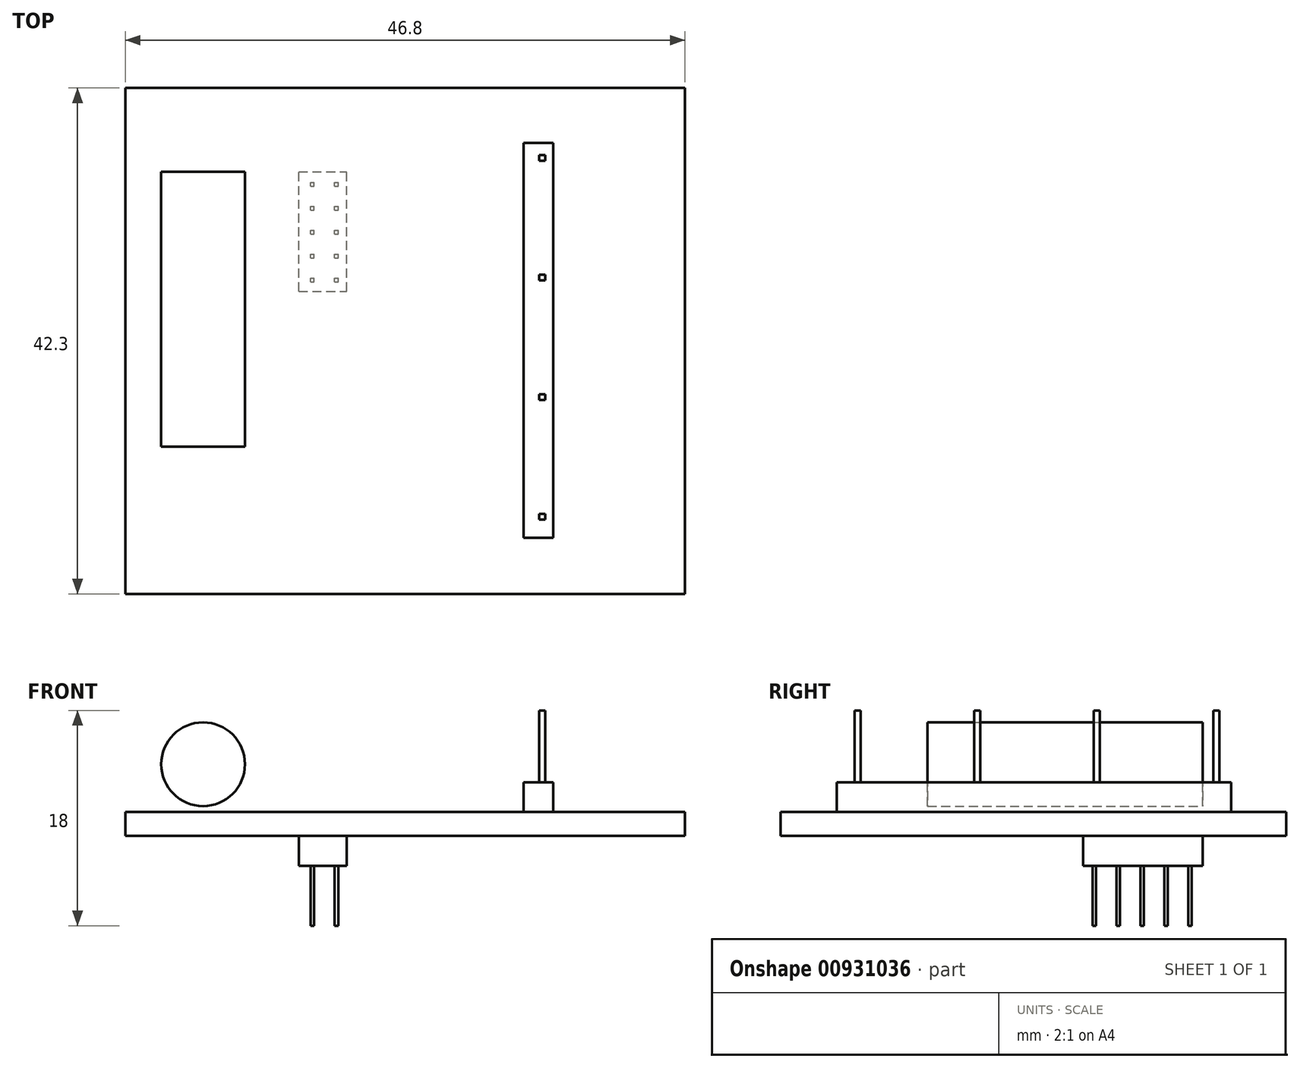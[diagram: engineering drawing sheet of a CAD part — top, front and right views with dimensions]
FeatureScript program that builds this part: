
annotation { "Feature Type Name" : "Feature", "Feature Type Description" : "" }
export const myFeature = defineFeature(function(context is Context, id is Id, definition is map)
    precondition{}
    {
        {
            assignVariable(context, id + "F0", {"name" : "PCB_WIDTH", "anyValue" : 42.3 * mm});
        }
        {
            assignVariable(context, id + "F1", {"name" : "PCB_HIGH", "anyValue" : 2 * mm});
        }
        {
            var Q0;
            Q0=qCreatedBy(makeId("Top.planeOp"),FACE);
            var sketch = newSketch(context, id + "F2", { "sketchPlane" : qUnion([Q0])});
            skLineSegment(sketch, "E0.bottom", {"start": v(-23.4, 21.15) * mm, "end": v(23.4, 21.15) * mm});
            skLineSegment(sketch, "E0.top", {"start": v(-23.4, -21.15) * mm, "end": v(23.4, -21.15) * mm});
            skLineSegment(sketch, "E0.left", {"start": v(-23.4, 21.15) * mm, "end": v(-23.4, -21.15) * mm});
            skLineSegment(sketch, "E0.right", {"start": v(23.4, 21.15) * mm, "end": v(23.4, -21.15) * mm});
            skLineSegment(sketch, "E1", {"start": v(-23.4, 21.15) * mm, "end": v(23.4, -21.15) * mm, "construction": true});
            skLineSegment(sketch, "E2", {"start": v(23.4, 21.15) * mm, "end": v(-23.4, -21.15) * mm, "construction": true});
            skPoint(sketch, "E3", {"position": v(0, 0) * mm});
            skSolve(sketch);
        }
        {
            var Q0;
            Q0 = qSketchRegion(id + "F2", true);
            extrude(context, id + "F3", {"entities" : qUnion([Q0]), "depth" : (getVariable(context, 'PCB_HIGH')), "offsetDistance" : 25 * mm});
        }
        {
            var Q0;
            Q0=qCreatedBy(makeId("Front.planeOp"),FACE);
            cPlane(context, id + "F4", {"entities" : qUnion([Q0]), "cplaneType" : CPlaneType.OFFSET, "offset" : (getVariable(context, 'PCB_WIDTH') / 2 - 7 * mm), "oppositeDirection" : true, "width" : 150 * mm, "height" : 150 * mm});
        }
        {
            var Q0;
            Q0=qCreatedBy(id+"F4.planeOp",FACE);
            var sketch = newSketch(context, id + "F5", { "sketchPlane" : qUnion([Q0])});
            skCircle(sketch, "E4", {"center": v(-16.9, 6) * mm, "radius": 3.5 * mm});
            skSolve(sketch);
        }
        {
            var Q0;
            Q0 = qSketchRegion(id + "F5", true);
            extrude(context, id + "F6", {"entities" : qUnion([Q0]), "depth" : 23 * mm, "offsetDistance" : 25 * mm});
        }
        {
            var Q0;
            Q0=makeQuery(id+"F3.opExtrude","CAP_FACE",FACE,{"disambiguationData":[OSD([sQuery(id+"F2.wireOp",EDGE,"E0.bottom"),sQuery(id+"F2.wireOp",EDGE,"E0.top"),sQuery(id+"F2.wireOp",EDGE,"E0.left"),sQuery(id+"F2.wireOp",EDGE,"E0.right")])],"isStart":false});
            var sketch = newSketch(context, id + "F7", { "sketchPlane" : qUnion([Q0])});
            skLineSegment(sketch, "E5.bottom", {"start": v(9.9, 16.55) * mm, "end": v(12.4, 16.55) * mm});
            skLineSegment(sketch, "E5.top", {"start": v(9.9, -16.45) * mm, "end": v(12.4, -16.45) * mm});
            skLineSegment(sketch, "E5.left", {"start": v(9.9, 16.55) * mm, "end": v(9.9, -16.45) * mm});
            skLineSegment(sketch, "E5.right", {"start": v(12.4, 16.55) * mm, "end": v(12.4, -16.45) * mm});
            skSolve(sketch);
        }
        {
            var Q0;
            Q0 = qSketchRegion(id + "F7", true);
            extrude(context, id + "F8", {"entities" : qUnion([Q0]), "depth" : 2.5 * mm, "offsetDistance" : 25 * mm});
        }
        {
            var Q0;
            Q0=makeQuery(id+"F8.opExtrude","CAP_FACE",FACE,{"disambiguationData":[OSD([sQuery(id+"F7.wireOp",EDGE,"E5.bottom"),sQuery(id+"F7.wireOp",EDGE,"E5.top"),sQuery(id+"F7.wireOp",EDGE,"E5.left"),sQuery(id+"F7.wireOp",EDGE,"E5.right")])],"isStart":false});
            var sketch = newSketch(context, id + "F9", { "sketchPlane" : qUnion([Q0])});
            skLineSegment(sketch, "E6.bottom", {"start": v(11.23, 15.55) * mm, "end": v(11.73, 15.55) * mm});
            skLineSegment(sketch, "E6.top", {"start": v(11.23, 15.05) * mm, "end": v(11.73, 15.05) * mm});
            skLineSegment(sketch, "E6.left", {"start": v(11.23, 15.55) * mm, "end": v(11.23, 15.05) * mm});
            skLineSegment(sketch, "E6.right", {"start": v(11.73, 15.55) * mm, "end": v(11.73, 15.05) * mm});
            skLineSegment(sketch, "E7.0.1.0", {"start": v(11.23, 5.05) * mm, "end": v(11.73, 5.05) * mm});
            skLineSegment(sketch, "E7.0.1.1", {"start": v(11.23, 5.55) * mm, "end": v(11.23, 5.05) * mm});
            skLineSegment(sketch, "E7.0.1.2", {"start": v(11.73, 5.55) * mm, "end": v(11.73, 5.05) * mm});
            skLineSegment(sketch, "E7.0.1.3", {"start": v(11.23, 5.55) * mm, "end": v(11.73, 5.55) * mm});
            skLineSegment(sketch, "E7.0.2.0", {"start": v(11.23, -4.95) * mm, "end": v(11.73, -4.95) * mm});
            skLineSegment(sketch, "E7.0.2.1", {"start": v(11.23, -4.45) * mm, "end": v(11.23, -4.95) * mm});
            skLineSegment(sketch, "E7.0.2.2", {"start": v(11.73, -4.45) * mm, "end": v(11.73, -4.95) * mm});
            skLineSegment(sketch, "E7.0.2.3", {"start": v(11.23, -4.45) * mm, "end": v(11.73, -4.45) * mm});
            skLineSegment(sketch, "E7.0.3.0", {"start": v(11.23, -14.95) * mm, "end": v(11.73, -14.95) * mm});
            skLineSegment(sketch, "E7.0.3.1", {"start": v(11.23, -14.45) * mm, "end": v(11.23, -14.95) * mm});
            skLineSegment(sketch, "E7.0.3.2", {"start": v(11.73, -14.45) * mm, "end": v(11.73, -14.95) * mm});
            skLineSegment(sketch, "E7.0.3.3", {"start": v(11.23, -14.45) * mm, "end": v(11.73, -14.45) * mm});
            skLineSegment(sketch, "E7.direction1", {"start": v(11.23, 15.05) * mm, "end": v(40.23, 15.05) * mm, "construction": true});
            skLineSegment(sketch, "E7.direction2", {"start": v(11.23, 15.05) * mm, "end": v(11.23, 5.05) * mm, "construction": true});
            skSolve(sketch);
        }
        {
            var Q0;
            Q0 = qSketchRegion(id + "F9", true);
            extrude(context, id + "F10", {"entities" : qUnion([Q0]), "depth" : 6 * mm, "offsetDistance" : 25 * mm});
        }
        {
            var Q0;
            Q0=makeQuery(id+"F3.opExtrude","CAP_FACE",FACE,{"disambiguationData":[OSD([sQuery(id+"F2.wireOp",EDGE,"E0.bottom"),sQuery(id+"F2.wireOp",EDGE,"E0.top"),sQuery(id+"F2.wireOp",EDGE,"E0.left"),sQuery(id+"F2.wireOp",EDGE,"E0.right")])],"isStart":true});
            var sketch = newSketch(context, id + "F11", { "sketchPlane" : qUnion([Q0])});
            skLineSegment(sketch, "E8.bottom", {"start": v(-8.9, -4.15) * mm, "end": v(-4.9, -4.15) * mm});
            skLineSegment(sketch, "E8.top", {"start": v(-8.9, -14.15) * mm, "end": v(-4.9, -14.15) * mm});
            skLineSegment(sketch, "E8.left", {"start": v(-8.9, -4.15) * mm, "end": v(-8.9, -14.15) * mm});
            skLineSegment(sketch, "E8.right", {"start": v(-4.9, -4.15) * mm, "end": v(-4.9, -14.15) * mm});
            skSolve(sketch);
        }
        {
            var Q0;
            Q0 = qSketchRegion(id + "F11", true);
            extrude(context, id + "F12", {"entities" : qUnion([Q0]), "depth" : 2.5 * mm, "offsetDistance" : 25 * mm});
        }
        {
            var Q0;
            Q0=makeQuery(id+"F12.opExtrude","CAP_FACE",FACE,{"disambiguationData":[OSD([sQuery(id+"F11.wireOp",EDGE,"E8.bottom"),sQuery(id+"F11.wireOp",EDGE,"E8.top"),sQuery(id+"F11.wireOp",EDGE,"E8.left"),sQuery(id+"F11.wireOp",EDGE,"E8.right")])],"isStart":false});
            var sketch = newSketch(context, id + "F13", { "sketchPlane" : qUnion([Q0])});
            skLineSegment(sketch, "E9.bottom", {"start": v(-7.9, -4.95) * mm, "end": v(-7.6, -4.95) * mm});
            skLineSegment(sketch, "E9.top", {"start": v(-7.9, -5.25) * mm, "end": v(-7.6, -5.25) * mm});
            skLineSegment(sketch, "E9.left", {"start": v(-7.9, -4.95) * mm, "end": v(-7.9, -5.25) * mm});
            skLineSegment(sketch, "E9.right", {"start": v(-7.6, -4.95) * mm, "end": v(-7.6, -5.25) * mm});
            skLineSegment(sketch, "E10.0.1.0", {"start": v(-7.9, -6.95) * mm, "end": v(-7.9, -7.25) * mm});
            skLineSegment(sketch, "E10.0.1.1", {"start": v(-7.9, -6.95) * mm, "end": v(-7.6, -6.95) * mm});
            skLineSegment(sketch, "E10.0.1.2", {"start": v(-7.6, -6.95) * mm, "end": v(-7.6, -7.25) * mm});
            skLineSegment(sketch, "E10.0.1.3", {"start": v(-7.9, -7.25) * mm, "end": v(-7.6, -7.25) * mm});
            skLineSegment(sketch, "E10.0.2.0", {"start": v(-7.9, -8.95) * mm, "end": v(-7.9, -9.25) * mm});
            skLineSegment(sketch, "E10.0.2.1", {"start": v(-7.9, -8.95) * mm, "end": v(-7.6, -8.95) * mm});
            skLineSegment(sketch, "E10.0.2.2", {"start": v(-7.6, -8.95) * mm, "end": v(-7.6, -9.25) * mm});
            skLineSegment(sketch, "E10.0.2.3", {"start": v(-7.9, -9.25) * mm, "end": v(-7.6, -9.25) * mm});
            skLineSegment(sketch, "E10.0.3.0", {"start": v(-7.9, -10.95) * mm, "end": v(-7.9, -11.25) * mm});
            skLineSegment(sketch, "E10.0.3.1", {"start": v(-7.9, -10.95) * mm, "end": v(-7.6, -10.95) * mm});
            skLineSegment(sketch, "E10.0.3.2", {"start": v(-7.6, -10.95) * mm, "end": v(-7.6, -11.25) * mm});
            skLineSegment(sketch, "E10.0.3.3", {"start": v(-7.9, -11.25) * mm, "end": v(-7.6, -11.25) * mm});
            skLineSegment(sketch, "E10.0.4.0", {"start": v(-7.9, -12.95) * mm, "end": v(-7.9, -13.25) * mm});
            skLineSegment(sketch, "E10.0.4.1", {"start": v(-7.9, -12.95) * mm, "end": v(-7.6, -12.95) * mm});
            skLineSegment(sketch, "E10.0.4.2", {"start": v(-7.6, -12.95) * mm, "end": v(-7.6, -13.25) * mm});
            skLineSegment(sketch, "E10.0.4.3", {"start": v(-7.9, -13.25) * mm, "end": v(-7.6, -13.25) * mm});
            skLineSegment(sketch, "E10.1.0.0", {"start": v(-5.9, -4.95) * mm, "end": v(-5.9, -5.25) * mm});
            skLineSegment(sketch, "E10.1.0.1", {"start": v(-5.9, -4.95) * mm, "end": v(-5.6, -4.95) * mm});
            skLineSegment(sketch, "E10.1.0.2", {"start": v(-5.6, -4.95) * mm, "end": v(-5.6, -5.25) * mm});
            skLineSegment(sketch, "E10.1.0.3", {"start": v(-5.9, -5.25) * mm, "end": v(-5.6, -5.25) * mm});
            skLineSegment(sketch, "E10.1.1.0", {"start": v(-5.9, -6.95) * mm, "end": v(-5.9, -7.25) * mm});
            skLineSegment(sketch, "E10.1.1.1", {"start": v(-5.9, -6.95) * mm, "end": v(-5.6, -6.95) * mm});
            skLineSegment(sketch, "E10.1.1.2", {"start": v(-5.6, -6.95) * mm, "end": v(-5.6, -7.25) * mm});
            skLineSegment(sketch, "E10.1.1.3", {"start": v(-5.9, -7.25) * mm, "end": v(-5.6, -7.25) * mm});
            skLineSegment(sketch, "E10.1.2.0", {"start": v(-5.9, -8.95) * mm, "end": v(-5.9, -9.25) * mm});
            skLineSegment(sketch, "E10.1.2.1", {"start": v(-5.9, -8.95) * mm, "end": v(-5.6, -8.95) * mm});
            skLineSegment(sketch, "E10.1.2.2", {"start": v(-5.6, -8.95) * mm, "end": v(-5.6, -9.25) * mm});
            skLineSegment(sketch, "E10.1.2.3", {"start": v(-5.9, -9.25) * mm, "end": v(-5.6, -9.25) * mm});
            skLineSegment(sketch, "E10.1.3.0", {"start": v(-5.9, -10.95) * mm, "end": v(-5.9, -11.25) * mm});
            skLineSegment(sketch, "E10.1.3.1", {"start": v(-5.9, -10.95) * mm, "end": v(-5.6, -10.95) * mm});
            skLineSegment(sketch, "E10.1.3.2", {"start": v(-5.6, -10.95) * mm, "end": v(-5.6, -11.25) * mm});
            skLineSegment(sketch, "E10.1.3.3", {"start": v(-5.9, -11.25) * mm, "end": v(-5.6, -11.25) * mm});
            skLineSegment(sketch, "E10.1.4.0", {"start": v(-5.9, -12.95) * mm, "end": v(-5.9, -13.25) * mm});
            skLineSegment(sketch, "E10.1.4.1", {"start": v(-5.9, -12.95) * mm, "end": v(-5.6, -12.95) * mm});
            skLineSegment(sketch, "E10.1.4.2", {"start": v(-5.6, -12.95) * mm, "end": v(-5.6, -13.25) * mm});
            skLineSegment(sketch, "E10.1.4.3", {"start": v(-5.9, -13.25) * mm, "end": v(-5.6, -13.25) * mm});
            skLineSegment(sketch, "E10.direction1", {"start": v(-7.9, -5.25) * mm, "end": v(-5.9, -5.25) * mm, "construction": true});
            skLineSegment(sketch, "E10.direction2", {"start": v(-7.9, -5.25) * mm, "end": v(-7.9, -7.25) * mm, "construction": true});
            skSolve(sketch);
        }
        {
            var Q0;
            Q0 = qSketchRegion(id + "F13", true);
            extrude(context, id + "F14", {"entities" : qUnion([Q0]), "depth" : 5 * mm, "offsetDistance" : 25 * mm});
        }
    });
